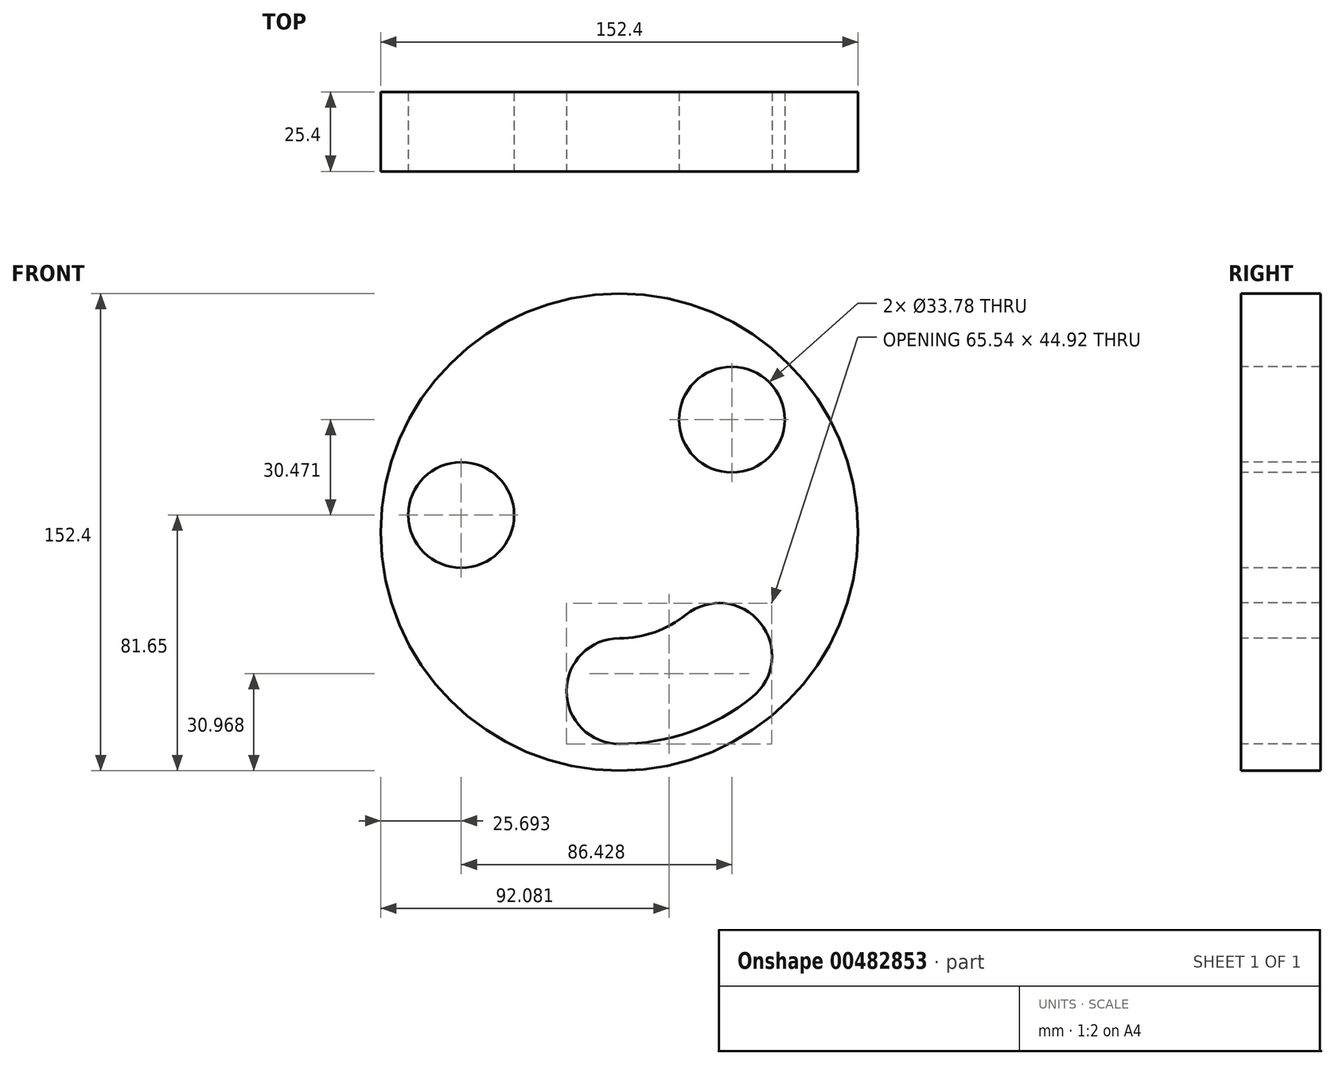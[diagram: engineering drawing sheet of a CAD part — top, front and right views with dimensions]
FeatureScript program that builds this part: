
annotation { "Feature Type Name" : "Feature", "Feature Type Description" : "" }
export const myFeature = defineFeature(function(context is Context, id is Id, definition is map)
    precondition{}
    {
        {
            var Q0;
            Q0=qCreatedBy(makeId("Front.planeOp"),FACE);
            var sketch = newSketch(context, id + "F0", { "sketchPlane" : qUnion([Q0])});
            skCircle(sketch, "E0", {"center": v(0, 0) * mm, "radius": 76.2 * mm});
            skSolve(sketch);
        }
        {
            var Q0;
            Q0 = qSketchRegion(id + "F0", true);
            extrude(context, id + "F1", {"entities" : qUnion([Q0]), "depth" : 25.4 * mm});
        }
        {
            var Q0;
            Q0=makeQuery(id+"F1.opExtrude","CAP_FACE",FACE,{"disambiguationData":[OSD([sQuery(id+"F0.wireOp",EDGE,"E0")])],"isStart":false});
            var sketch = newSketch(context, id + "F2", { "sketchPlane" : qUnion([Q0])});
            skCircle(sketch, "E1", {"center": v(0, 50.8) * mm, "radius": 15.88 * mm});
            skCircle(sketch, "E2.1.0", {"center": v(-35.92, 35.92) * mm, "radius": 15.88 * mm});
            skCircle(sketch, "E2.2.0", {"center": v(-50.8, 0) * mm, "radius": 15.88 * mm});
            skCircle(sketch, "E2.3.0", {"center": v(-35.92, -35.92) * mm, "radius": 15.88 * mm});
            skCircle(sketch, "E2.4.0", {"center": v(0, -50.8) * mm, "radius": 15.88 * mm});
            skCircle(sketch, "E2.5.0", {"center": v(35.92, -35.92) * mm, "radius": 15.88 * mm});
            skCircle(sketch, "E2.6.0", {"center": v(50.8, 0) * mm, "radius": 15.88 * mm});
            skCircle(sketch, "E2.7.0", {"center": v(35.92, 35.92) * mm, "radius": 15.88 * mm});
            skPoint(sketch, "E2.center", {"position": v(0, 0) * mm});
            skSolve(sketch);
        }
        {
            var Q0;
            Q0=makeQuery(id+"F2.imprint","IMPRINT",FACE,{"disambiguationData":[TD([[makeQuery(id+"F2.imprint","IMPRINT",EDGE,{"derivedFrom":sQuery(id+"F2.wireOp",EDGE,"E1")}),-1.0]])]});
            var sketch = newSketch(context, id + "F3", { "sketchPlane" : qUnion([Q0])});
            skCircle(sketch, "E3", {"center": v(35.92, 35.92) * mm, "radius": 16.9 * mm});
            skArc(sketch, "E4", {"start": v(0, -33.9) * mm, "mid": v(-16.9, -50.8) * mm, "end": v(0, -67.7) * mm});
            skCircle(sketch, "E5", {"center": v(-50.5, 5.45) * mm, "radius": 16.9 * mm});
            skArc(sketch, "E6", {"start": v(42.45, -52.72) * mm, "mid": v(45.02, -28.97) * mm, "end": v(21.27, -26.41) * mm});
            skArc(sketch, "E7", {"start": v(0, -67.7) * mm, "mid": v(22.5, -63.84) * mm, "end": v(42.45, -52.72) * mm});
            skArc(sketch, "E8", {"start": v(0, -33.9) * mm, "mid": v(11.27, -31.98) * mm, "end": v(21.27, -26.41) * mm});
            skSolve(sketch);
        }
        {
            var Q0;
            Q0 = qSketchRegion(id + "F3", true);
            extrude(context, id + "F4", {"entities" : qUnion([Q0]), "operationType" : NewBodyOperationType.REMOVE, "oppositeDirection" : true, "depth" : 25.4 * mm});
        }
    });
